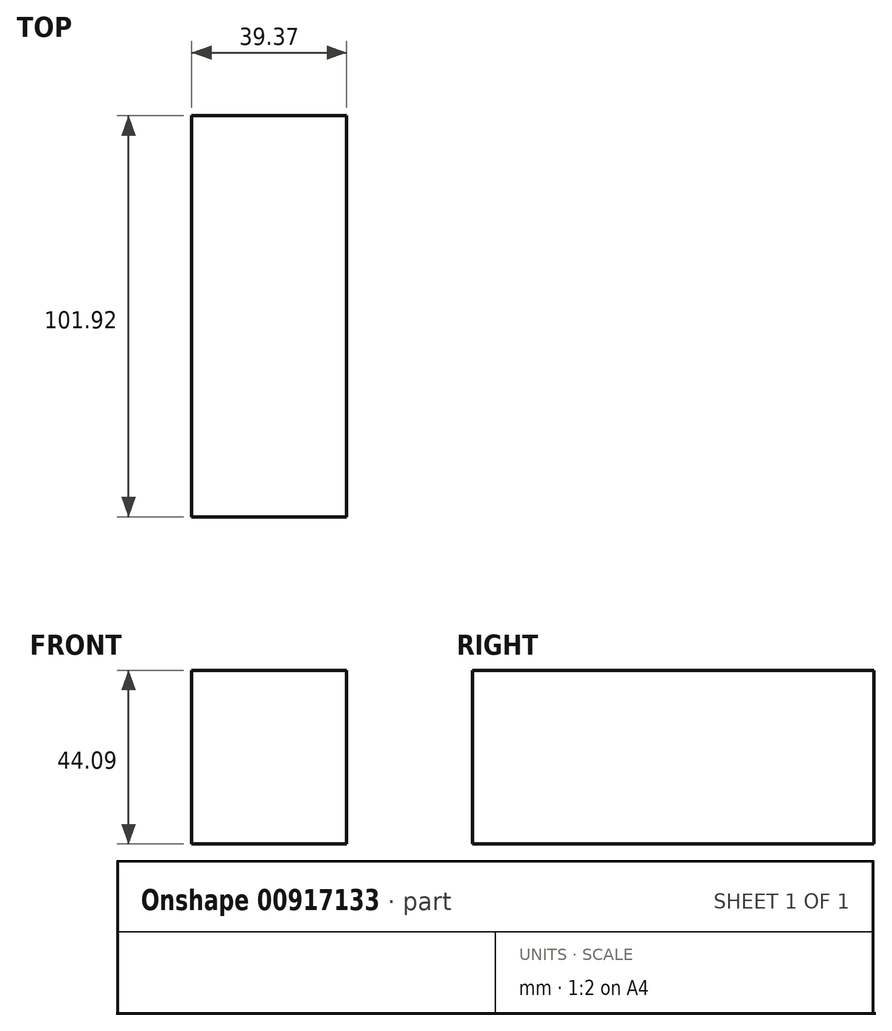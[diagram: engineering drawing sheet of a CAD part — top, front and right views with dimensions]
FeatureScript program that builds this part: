
annotation { "Feature Type Name" : "Feature", "Feature Type Description" : "" }
export const myFeature = defineFeature(function(context is Context, id is Id, definition is map)
    precondition{}
    {
        {
            var Q0;
            Q0=qCreatedBy(makeId("Right.planeOp"),FACE);
            var sketch = newSketch(context, id + "F0", { "sketchPlane" : qUnion([Q0])});
            skLineSegment(sketch, "E0.bottom", {"start": v(50.96, 24.1) * mm, "end": v(-50.96, 24.1) * mm});
            skLineSegment(sketch, "E0.top", {"start": v(50.96, -20) * mm, "end": v(-50.96, -20) * mm});
            skLineSegment(sketch, "E0.left", {"start": v(50.96, 24.1) * mm, "end": v(50.96, -20) * mm});
            skLineSegment(sketch, "E0.right", {"start": v(-50.96, 24.1) * mm, "end": v(-50.96, -20) * mm});
            skSolve(sketch);
        }
        {
            var Q0;
            Q0=makeQuery(id+"F0.imprint","IMPRINT",FACE,{"disambiguationData":[TD([[makeQuery(id+"F0.imprint","IMPRINT",EDGE,{"derivedFrom":sQuery(id+"F0.wireOp",EDGE,"E0.bottom")}),1.0]])]});
            extrude(context, id + "F1", {"entities" : qUnion([Q0]), "depth" : 39.37 * mm, "offsetDistance" : 25.4 * mm});
        }
    });
